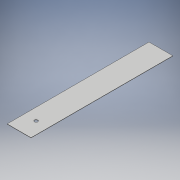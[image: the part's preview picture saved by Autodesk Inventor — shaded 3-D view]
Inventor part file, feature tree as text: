
AUTODESK INVENTOR PART (.ipt)
format: ipt  version: 2019 (Build 230136000, 136)  size: 105,984 bytes
history: native  units: mm
features: sketch x2, sheet_metal_op x1, hole x1, other x1
ambient origin geometry x8: Origin, YZ Plane, XZ Plane, XY Plane, X Axis, Y Axis, Z Axis, Center Point
bodies: Solid1 (feature_tree)
feature tree (5):
  sheet_metal_op  "Face1"
  hole  "Hole1"  [1 undecoded]
  sketch  "Sketch1"  dims[d0=42.0mm d1=250.0mm]
  other  "Plate1"
  sketch  "Sketch2"  dims[d2=0.5mm d3=21.0mm d4=30.0mm d5=6.0mm d6=6.0mm d7=4.0mm d8=2.0mm d9=90.0deg d10=0.5mm d11=20.594885mm]
note: 1 required parameter value undecoded (feature->parameter linkage not recoverable at this tier; creation-order binding heuristic only, values carry confidence <= 0.55)
